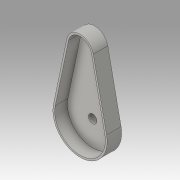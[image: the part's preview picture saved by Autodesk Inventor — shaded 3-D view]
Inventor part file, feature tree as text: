
AUTODESK INVENTOR PART (.ipt)
format: ipt  version: 2016 (Build 200138000, 138)  size: 112,640 bytes
history: native  units: in
note: dims shown in document units (in); Inventor stores cm internally (conversion verified against a paired STEP export)
features: extrude x2, sketch x2, shell x1, hole x1
ambient origin geometry x8: Origin, YZ Plane, XZ Plane, XY Plane, X Axis, Y Axis, Z Axis, Center Point
bodies: Solid1 (feature_tree)
feature tree (6):
  extrude  "Extrusion1"  Depth=1.5in
  shell  "Shell1"  Thickness=5.9in
  extrude  "Extrusion2"  Depth=0.1in
  hole  "Hole1"  [1 undecoded]
  sketch  "Sketch1"  dims[d0=3.0in d1=1.5in d2=5.9in]
  sketch  "Sketch2"  dims[d3=0.8in d4=0.0in d5=0.1in d6=0.47in d7=0.85in d8=0.3in d9=0.0in d10=1.0in d11=1.0in d12=0.47in d13=0.75in d14=0.375in d15=0.25in d16=0.5635in d17=1.0in d18=0.8108in]
note: 1 required parameter value undecoded (feature->parameter linkage not recoverable at this tier; creation-order binding heuristic only, values carry confidence <= 0.55)
